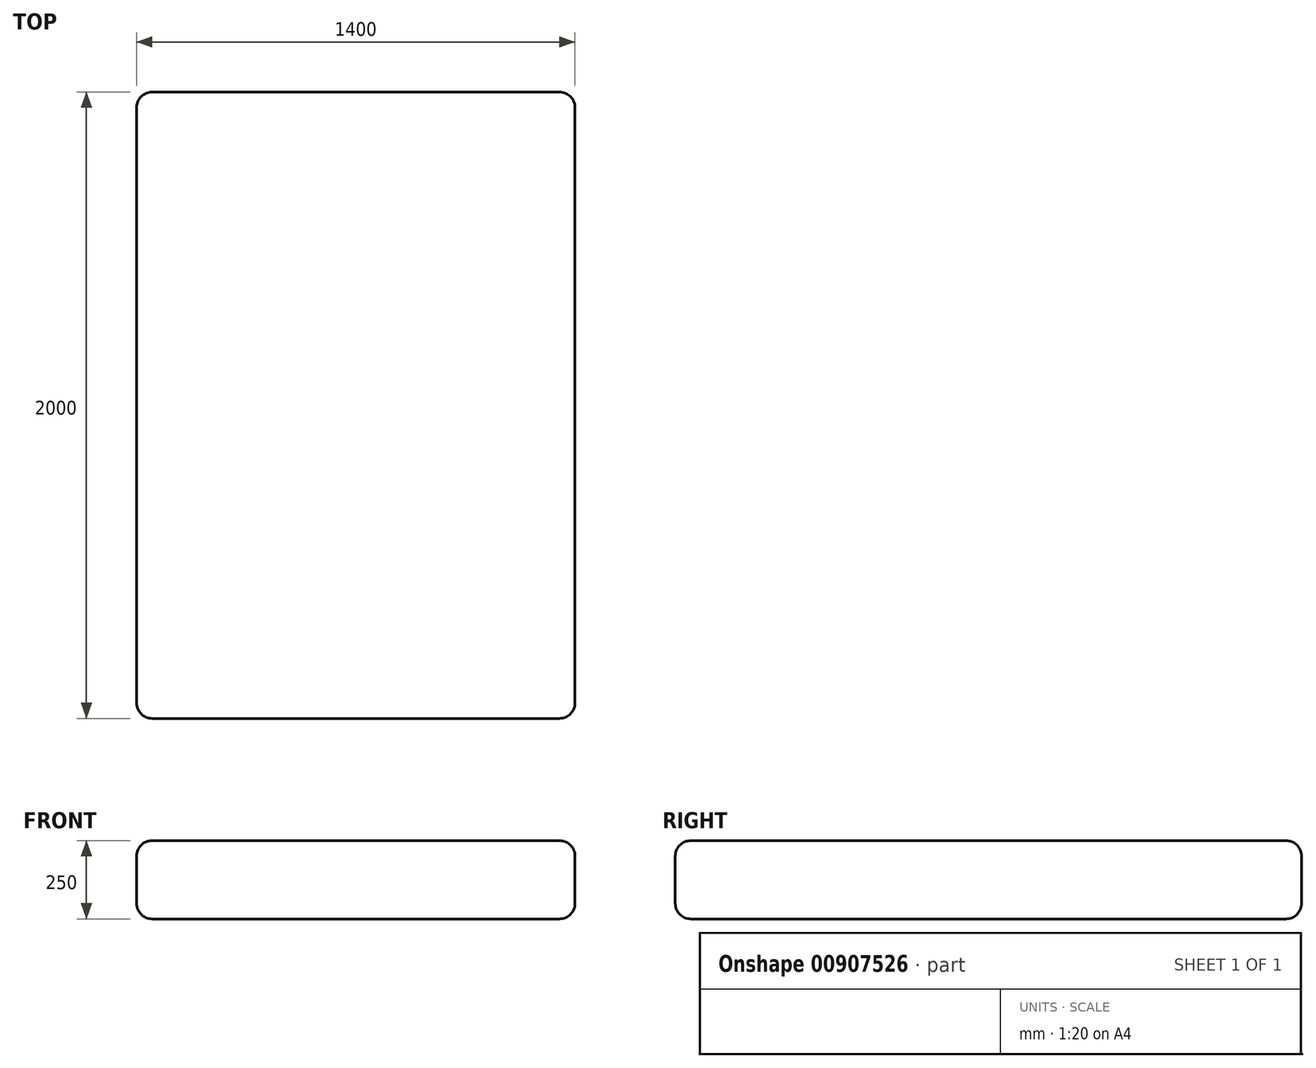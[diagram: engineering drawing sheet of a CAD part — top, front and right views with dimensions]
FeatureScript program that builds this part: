
annotation { "Feature Type Name" : "Feature", "Feature Type Description" : "" }
export const myFeature = defineFeature(function(context is Context, id is Id, definition is map)
    precondition{}
    {
        {
            var Q0;
            Q0=qCreatedBy(makeId("Top.planeOp"),FACE);
            var sketch = newSketch(context, id + "F0", { "sketchPlane" : qUnion([Q0])});
            skLineSegment(sketch, "E0.bottom", {"start": v(3.28, 0) * mm, "end": v(1403.28, 0) * mm});
            skLineSegment(sketch, "E0.top", {"start": v(3.28, -2000) * mm, "end": v(1403.28, -2000) * mm});
            skLineSegment(sketch, "E0.left", {"start": v(3.28, 0) * mm, "end": v(3.28, -2000) * mm});
            skLineSegment(sketch, "E0.right", {"start": v(1403.28, 0) * mm, "end": v(1403.28, -2000) * mm});
            skSolve(sketch);
        }
        {
            var Q0;
            Q0=qSketchRegion(id+"F0",true);
            extrude(context, id + "F1", {"entities" : qUnion([Q0]), "depth" : 250 * mm, "offsetDistance" : 25.4 * mm});
        }
        {
            var Q0;
            Q0=makeQuery(id+"F1.opExtrude","CAP_EDGE",EDGE,{"disambiguationData":[OSD([sQuery(id+"F0.wireOp",EDGE,"E0.top")])],"isStart":false});
            var Q1;
            Q1=makeQuery(id+"F1.opExtrude","CAP_EDGE",EDGE,{"disambiguationData":[OSD([sQuery(id+"F0.wireOp",EDGE,"E0.right")])],"isStart":false});
            var Q2;
            Q2=makeQuery(id+"F1.opExtrude","SWEPT_EDGE",EDGE,{"disambiguationData":[OSD([sQuery(id+"F0.wireOp",EDGE,"E0.top"),sQuery(id+"F0.wireOp",EDGE,"E0.right")])]});
            var Q3;
            Q3=makeQuery(id+"F1.opExtrude","SWEPT_EDGE",EDGE,{"disambiguationData":[OSD([sQuery(id+"F0.wireOp",EDGE,"E0.top"),sQuery(id+"F0.wireOp",EDGE,"E0.left")])]});
            var Q4;
            Q4=makeQuery(id+"F1.opExtrude","CAP_EDGE",EDGE,{"disambiguationData":[OSD([sQuery(id+"F0.wireOp",EDGE,"E0.top")])],"isStart":true});
            var Q5;
            Q5=makeQuery(id+"F1.opExtrude","CAP_EDGE",EDGE,{"disambiguationData":[OSD([sQuery(id+"F0.wireOp",EDGE,"E0.right")])],"isStart":true});
            var Q6;
            Q6=makeQuery(id+"F1.opExtrude","SWEPT_EDGE",EDGE,{"disambiguationData":[OSD([sQuery(id+"F0.wireOp",EDGE,"E0.bottom"),sQuery(id+"F0.wireOp",EDGE,"E0.right")])]});
            var Q7;
            Q7=makeQuery(id+"F1.opExtrude","CAP_EDGE",EDGE,{"disambiguationData":[OSD([sQuery(id+"F0.wireOp",EDGE,"E0.bottom")])],"isStart":true});
            var Q8;
            Q8=makeQuery(id+"F1.opExtrude","CAP_EDGE",EDGE,{"disambiguationData":[OSD([sQuery(id+"F0.wireOp",EDGE,"E0.bottom")])],"isStart":false});
            var Q9;
            Q9=makeQuery(id+"F1.opExtrude","SWEPT_EDGE",EDGE,{"disambiguationData":[OSD([sQuery(id+"F0.wireOp",EDGE,"E0.bottom"),sQuery(id+"F0.wireOp",EDGE,"E0.left")])]});
            var Q10;
            Q10=makeQuery(id+"F1.opExtrude","CAP_EDGE",EDGE,{"disambiguationData":[OSD([sQuery(id+"F0.wireOp",EDGE,"E0.left")])],"isStart":false});
            var Q11;
            Q11=makeQuery(id+"F1.opExtrude","CAP_EDGE",EDGE,{"disambiguationData":[OSD([sQuery(id+"F0.wireOp",EDGE,"E0.left")])],"isStart":true});
            fillet(context, id + "F2", {"entities" : qUnion([Q0, Q1, Q2, Q3, Q4, Q5, Q6, Q7, Q8, Q9, Q10, Q11]), "radius" : 50 * mm, "tangentPropagation" : true, "allowEdgeOverflow" : false});
        }
    });
